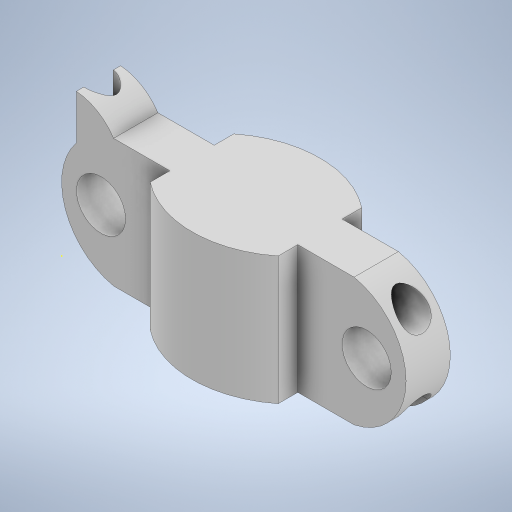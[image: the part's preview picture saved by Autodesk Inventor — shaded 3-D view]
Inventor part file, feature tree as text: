
AUTODESK INVENTOR PART (.ipt)
format: ipt  version: 2023 (Build 270158000, 158)  size: 364,544 bytes
history: native  units: in
note: dims shown in document units (in); Inventor stores cm internally (conversion verified against a paired STEP export)
features: extrude x8, sketch x7, projected_geometry x2, plane x1
ambient origin geometry x8: Origin, YZ Plane, XZ Plane, XY Plane, X Axis, Y Axis, Z Axis, Center Point
bodies: Solid1 (feature_tree)
feature tree (18):
  sketch  "Sketch1"  dims[d0=1.378in d1=0.5118in]
  extrude  "Extrusion1"  Depth=0.5118in
  extrude  "Extrusion2"  Depth=0.1969in
  sketch  "Sketch2"  dims[d2=0.315in d3=0.1969in]
  plane  "Work Plane2"
  extrude  "Extrusion7"  Depth=0.5118in TaperAngle=0.0deg
  extrude  "Extrusion8"  Depth=0.0787in
  extrude  "Extrusion9"  Depth=0.0787in
  sketch  "Sketch7"  dims[d11=0.0787in d12=0.0787in]
  sketch  "Sketch8"  dims[d26=0.1181in d27=0.0in d28=0.0in]
  extrude  "Extrusion10"  TaperAngle=0.0deg  [1 undecoded]
  extrude  "Extrusion11"  Depth=0.1969in
  extrude  "Extrusion12"  Depth=0.1969in
  projected_geometry  "Projected Loop1"
  sketch  "Sketch5"  dims[d5=0.1772in d6=0.0in d7=0.5118in d8=0.0in]
  sketch  "Sketch6"  dims[d9=0.0787in d10=0.0787in]
  sketch  "Sketch9"  dims[d29=0.3937in d30=0.0in d31=0.0787in d32=0.0787in d33=0.0in d34=0.0in d35=0.0886in d36=0.0in d37=0.0886in d38=0.0in d39=0.1969in d40=0.0in d41=0.0in]
  projected_geometry  "Projected Loop4"
note: 1 required parameter value undecoded (feature->parameter linkage not recoverable at this tier; creation-order binding heuristic only, values carry confidence <= 0.55)
